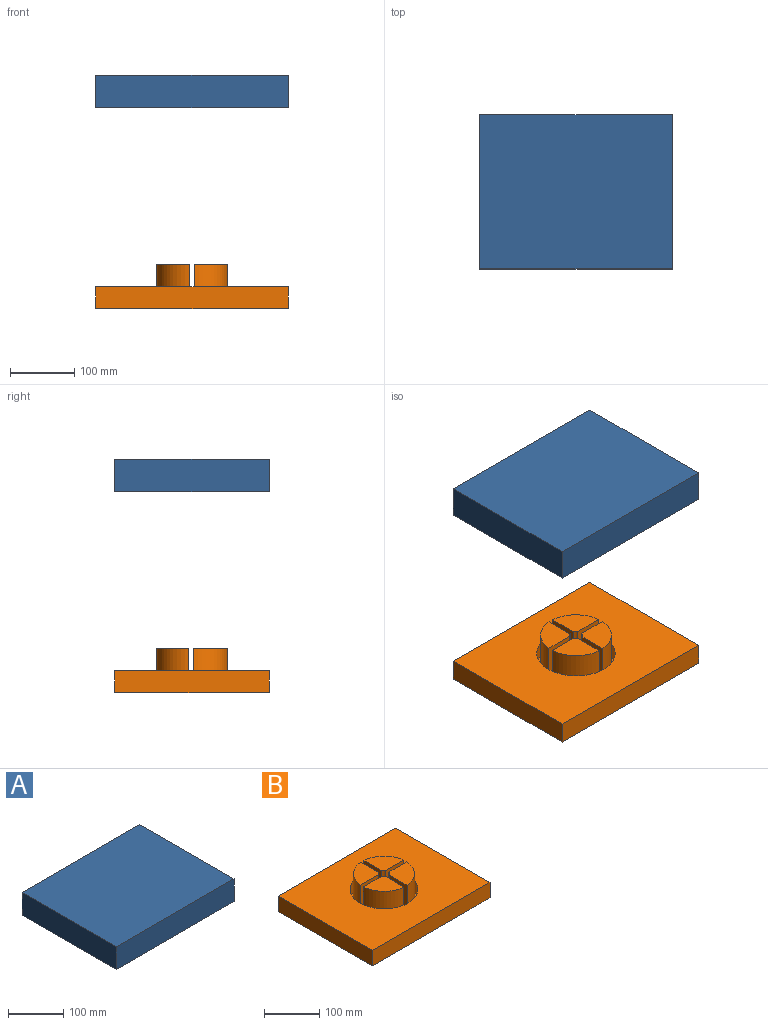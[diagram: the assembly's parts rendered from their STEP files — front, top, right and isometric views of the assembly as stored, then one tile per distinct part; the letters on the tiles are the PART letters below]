
ASSEMBLY  parts=2 mates=2
PART A: 8 faces, bbox 300.9x240.4x50.3 mm
  f0: plane 300.94x50.29mm, normal (0,-1,0), area 15134.8mm2, adj f1,f4,f5,f7
  f1: plane 240.44x50.29mm, normal (1,0,0), area 12092mm2, adj f0,f2,f5,f7
  f2: plane 300.94x50.29mm, normal (0,1,0), area 15134.8mm2, adj f1,f4,f5,f7
  f3: cylinder r=61.25mm len=122.5mm, axis (0,0,-1), area 14663.1mm2, adj f5,f6
  f4: plane 240.44x50.29mm, normal (-1,0,0), area 12092mm2, adj f0,f2,f5,f7
  f5: plane 300.94x240.44mm, normal (0,0,-1), area 60570mm2, adj f0,f1,f2,f3,f4
  f6: plane 122.5x122.5mm, normal (0,0,-1), area 11786.7mm2, adj f3
  f7: plane 300.94x240.44mm, normal (0,0,1), area 72356.7mm2, adj f0,f1,f2,f4
PART B: 28 faces, bbox 300.9x240.4x68.6 mm
  f0: plane 122.49x122.49mm, normal (0,0,1), area 3942.1mm2, adj f1,f2,f3,f4,f6,f7,f8,f9
  f1: cylinder r=55.21mm len=59.69mm, axis (0,0,-1), area 4645.3mm2, adj f0,f2,f4,f5
  f2: plane 59.69x45.78mm, normal (-1,0,0), area 2732.3mm2, adj f0,f1,f3,f5
  f3: cylinder r=10.05mm len=59.69mm, axis (0,0,-1), area 391.3mm2, adj f0,f2,f4,f5
  f4: plane 59.69x46.3mm, normal (0,-1,0), area 2763.9mm2, adj f0,f1,f3,f5
  f5: plane 51.17x49.99mm, normal (0,0,1), area 1910.6mm2, adj f1,f2,f3,f4
  f6: plane 59.69x45.84mm, normal (1,0,0), area 2736.3mm2, adj f0,f7,f9,f10
  f7: cylinder r=55.21mm len=59.69mm, axis (0,0,-1), area 4634mm2, adj f0,f6,f8,f10
  f8: plane 59.69x46.3mm, normal (0,-1,0), area 2763.9mm2, adj f0,f7,f9,f10
  f9: cylinder r=10.05mm len=59.69mm, axis (0,0,-1), area 379.1mm2, adj f0,f6,f8,f10
  f10: plane 50.98x49.98mm, normal (0,0,1), area 1901.9mm2, adj f6,f7,f8,f9
  f11: plane 59.69x45.84mm, normal (1,0,0), area 2736.3mm2, adj f0,f12,f14,f15
  f12: cylinder r=10.05mm len=59.69mm, axis (0,0,-1), area 533.4mm2, adj f0,f11,f13,f15
  f13: plane 59.69x45.46mm, normal (0,1,0), area 2713.8mm2, adj f0,f12,f14,f15
  f14: cylinder r=55.21mm len=59.69mm, axis (0,0,-1), area 4776mm2, adj f0,f11,f13,f15
  f15: plane 52.35x51.15mm, normal (0,0,1), area 2010.7mm2, adj f11,f12,f13,f14
  f16: cylinder r=10.05mm len=59.69mm, axis (0,0,-1), area 545.6mm2, adj f0,f17,f19,f20
  f17: plane 59.69x45.78mm, normal (-1,0,0), area 2732.3mm2, adj f0,f16,f18,f20
  f18: cylinder r=55.21mm len=59.69mm, axis (0,0,-1), area 4787.3mm2, adj f0,f17,f19,f20
  f19: plane 59.69x45.46mm, normal (0,1,0), area 2713.8mm2, adj f0,f16,f18,f20
  f20: plane 52.37x51.34mm, normal (0,0,1), area 2019.3mm2, adj f16,f17,f18,f19
  f21: cylinder r=61.25mm len=122.49mm, axis (0,0,-1), area 9774.5mm2, adj f0,f22
  f22: plane 300.95x240.43mm, normal (0,0,1), area 60571.5mm2, adj f21,f24,f25,f26,f27
  f23: plane 300.95x240.43mm, normal (0,0,-1), area 72356.1mm2, adj f24,f25,f26,f27
  f24: plane 240.43x34.29mm, normal (1,0,0), area 8244.3mm2, adj f22,f23,f25,f27
  f25: plane 300.95x34.29mm, normal (0,-1,0), area 10319.5mm2, adj f22,f23,f24,f26
  f26: plane 240.43x34.29mm, normal (-1,0,0), area 8244.3mm2, adj f22,f23,f25,f27
  f27: plane 300.95x34.29mm, normal (0,1,0), area 10319.5mm2, adj f22,f23,f24,f26
PLACE A t=(0,0,304.39)mm
PLACE B at identity fixed
MATE planar A.f0 <-> B.f25  axis (0,-1,0) through (0,-120.21,329.54)mm
MATE planar A.f1 <-> B.f24  axis (1,0,0) through (150.47,0,329.54)mm
